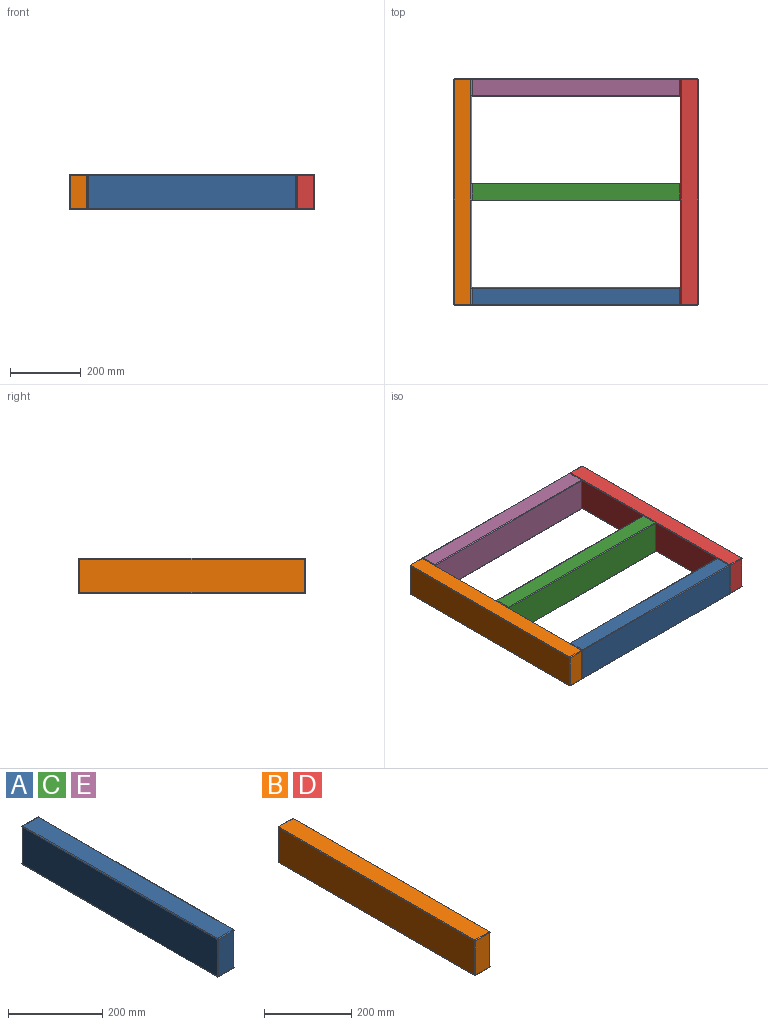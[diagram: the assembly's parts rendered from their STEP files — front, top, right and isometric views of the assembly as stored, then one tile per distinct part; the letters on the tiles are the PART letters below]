
ASSEMBLY  parts=5 mates=9
PART A: 26 faces, bbox 50x590x100 mm
  f0: plane 586x46mm, normal (0,0,-1), area 26956mm2, adj f14,f19,f22,f25
  f1: plane 586x96mm, normal (1,0,0), area 56256mm2, adj f11,f20,f21,f25
  f2: plane 586x46mm, normal (0,0,1), area 26956mm2, adj f6,f10,f11,f12
  f3: plane 586x96mm, normal (-1,0,0), area 56256mm2, adj f6,f9,f13,f14
  f4: plane 96x46mm, normal (0,-1,0), area 4416mm2, adj f9,f10,f19,f20
  f5: plane 96x46mm, normal (0,1,0), area 4416mm2, adj f12,f13,f21,f22
  f6: cylinder r=2mm len=586mm, axis (0,1,0), area 1841mm2, adj f2,f3,f7,f8
  f7: sphere r=2mm, area 6.3mm2, adj f6,f9,f10
  f8: sphere r=2mm, area 6.3mm2, adj f6,f12,f13
  f9: cylinder r=2mm len=96mm, axis (0,0,1), area 301.6mm2, adj f3,f4,f7,f15
  f10: cylinder r=2mm len=46mm, axis (1,0,0), area 144.5mm2, adj f2,f4,f7,f16
  f11: cylinder r=2mm len=586mm, axis (0,-1,0), area 1841mm2, adj f1,f2,f16,f17
  f12: cylinder r=2mm len=46mm, axis (-1,0,0), area 144.5mm2, adj f2,f5,f8,f17
  f13: cylinder r=2mm len=96mm, axis (0,0,-1), area 301.6mm2, adj f3,f5,f8,f18
  f14: cylinder r=2mm len=586mm, axis (0,-1,0), area 1841mm2, adj f0,f3,f15,f18
  f15: sphere r=2mm, area 6.3mm2, adj f9,f14,f19
  f16: sphere r=2mm, area 6.3mm2, adj f10,f11,f20
  f17: sphere r=2mm, area 6.3mm2, adj f11,f12,f21
  f18: sphere r=2mm, area 6.3mm2, adj f13,f14,f22
  f19: cylinder r=2mm len=46mm, axis (-1,0,0), area 144.5mm2, adj f0,f4,f15,f23
  f20: cylinder r=2mm len=96mm, axis (0,0,-1), area 301.6mm2, adj f1,f4,f16,f23
  f21: cylinder r=2mm len=96mm, axis (0,0,1), area 301.6mm2, adj f1,f5,f17,f24
  f22: cylinder r=2mm len=46mm, axis (1,0,0), area 144.5mm2, adj f0,f5,f18,f24
  f23: sphere r=2mm, area 6.3mm2, adj f19,f20,f25
  f24: sphere r=2mm, area 6.3mm2, adj f21,f22,f25
  f25: cylinder r=2mm len=586mm, axis (0,1,0), area 1841mm2, adj f0,f1,f23,f24
PART B: 26 faces, bbox 50x640x100 mm
  f0: plane 636x46mm, normal (0,0,-1), area 29256mm2, adj f14,f19,f22,f25
  f1: plane 636x96mm, normal (1,0,0), area 61056mm2, adj f11,f20,f21,f25
  f2: plane 636x46mm, normal (0,0,1), area 29256mm2, adj f6,f10,f11,f12
  f3: plane 636x96mm, normal (-1,0,0), area 61056mm2, adj f6,f9,f13,f14
  f4: plane 96x46mm, normal (0,-1,0), area 4416mm2, adj f9,f10,f19,f20
  f5: plane 96x46mm, normal (0,1,0), area 4416mm2, adj f12,f13,f21,f22
  f6: cylinder r=2mm len=636mm, axis (0,1,0), area 1998.1mm2, adj f2,f3,f7,f8
  f7: sphere r=2mm, area 6.3mm2, adj f6,f9,f10
  f8: sphere r=2mm, area 6.3mm2, adj f6,f12,f13
  f9: cylinder r=2mm len=96mm, axis (0,0,1), area 301.6mm2, adj f3,f4,f7,f15
  f10: cylinder r=2mm len=46mm, axis (1,0,0), area 144.5mm2, adj f2,f4,f7,f16
  f11: cylinder r=2mm len=636mm, axis (0,-1,0), area 1998.1mm2, adj f1,f2,f16,f17
  f12: cylinder r=2mm len=46mm, axis (-1,0,0), area 144.5mm2, adj f2,f5,f8,f17
  f13: cylinder r=2mm len=96mm, axis (0,0,-1), area 301.6mm2, adj f3,f5,f8,f18
  f14: cylinder r=2mm len=636mm, axis (0,-1,0), area 1998.1mm2, adj f0,f3,f15,f18
  f15: sphere r=2mm, area 6.3mm2, adj f9,f14,f19
  f16: sphere r=2mm, area 6.3mm2, adj f10,f11,f20
  f17: sphere r=2mm, area 6.3mm2, adj f11,f12,f21
  f18: sphere r=2mm, area 6.3mm2, adj f13,f14,f22
  f19: cylinder r=2mm len=46mm, axis (-1,0,0), area 144.5mm2, adj f0,f4,f15,f23
  f20: cylinder r=2mm len=96mm, axis (0,0,-1), area 301.6mm2, adj f1,f4,f16,f23
  f21: cylinder r=2mm len=96mm, axis (0,0,1), area 301.6mm2, adj f1,f5,f17,f24
  f22: cylinder r=2mm len=46mm, axis (1,0,0), area 144.5mm2, adj f0,f5,f18,f24
  f23: sphere r=2mm, area 6.3mm2, adj f19,f20,f25
  f24: sphere r=2mm, area 6.3mm2, adj f21,f22,f25
  f25: cylinder r=2mm len=636mm, axis (0,1,0), area 1998.1mm2, adj f0,f1,f23,f24
PART C: same geometry as A
PART D: same geometry as B
PART E: same geometry as A
PLACE A rot(axis=(-0.71,-0.71,0),180deg) t=(-312.61,-294.85,-6.17)mm
PLACE B t=(-632.61,0.15,-6.17)mm
PLACE C rot(axis=(0,0,1),90deg) t=(-312.61,0.15,-6.17)mm
PLACE D t=(7.39,0.15,-6.17)mm fixed
PLACE E rot(axis=(0,0,1),90deg) t=(-312.61,295.15,-6.17)mm
MATE planar A.f5 <-> D.f3  axis (1,0,0) through (-17.61,-294.85,-6.17)mm
MATE planar C.f4 <-> D.f3  axis (1,0,0) through (-17.61,0.15,-6.17)mm
MATE planar E.f4 <-> D.f3  axis (1,0,0) through (-17.61,295.15,-6.17)mm
MATE planar E.f2 <-> D.f2  axis (0,0,1) through (-312.61,295.15,43.83)mm
MATE planar A.f0 <-> D.f2  axis (0,0,1) through (-312.61,-294.85,43.83)mm
MATE planar B.f1 <-> C.f5  axis (1,0,0) through (-607.61,0.15,-6.17)mm
MATE planar A.f3 <-> D.f4  axis (0,-1,0) through (-312.61,-319.85,-6.17)mm
MATE planar C.f2 <-> D.f2  axis (0,0,1) through (-312.61,0.15,43.83)mm
MATE planar E.f1 <-> D.f5  axis (0,1,0) through (-312.61,320.15,-6.17)mm
